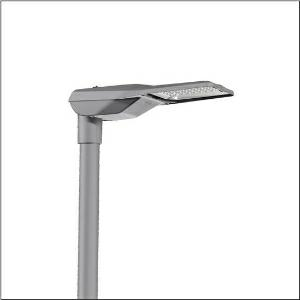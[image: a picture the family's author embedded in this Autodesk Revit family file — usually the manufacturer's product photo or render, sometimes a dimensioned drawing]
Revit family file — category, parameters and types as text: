
# Revit family: streetlight_sl_21_mini___pl52_5xe2h43s08hb_f567
name_source: partatom
category: Lighting Fixtures
units: mm (PartAtom-declared; Revit-internal decimal feet)

## family parameters
Cut with Voids When Loaded = No
Host = Face
Light Source = No
Part Type = Normal
Room Calculation Point = No
Round Connector Dimension = Use Diameter
Shared = No

## types (1)
- --- (1 x LED, 9260 lm, 66 W, 4000K)
    Apparent Load = 66 VA
    CIE Flux Codes = 27 59 98 100 100
    Color Rendering = 70
    Color Temperature = 4000K
    Default Elevation = 1800 mm
    Description = Streetlight SL 21 mini, mast luminaire, primary light control with lens, of PMMA, primary optical cover: cover, of toughened safety glass, transparent, light distribution: PL52, light emission: direct distribution, primary light characteristic: asymmetric, installation type: side-entry, post-top, LED, High Power LED, rated luminous flux: 9.260lm, luminous efficacy: 140lm/W, light colour: 740, colour temperature: 4000K, control gear: D4i, control: overheat protection, constant luminous flux control, time-dependent luminous flux control, flexible luminous flux parameterisation, pre-setting: logarithmic dimming characteristic, mains connection: 220..240V, AC, 50/60Hz, start of lifetime: 66W, end of service life: 69W, reduction: 30W, luminaire housing, of diecast aluminium, powder-coated, Siteco® metallic grey (DB 702S), corrosivity category C5 mid according to DIN EN ISO 12944, please order mast flange separately, inclination adjustable: 0°, 5°, 10°, 15°, sealing non-destructively replaceable, multi-level sealing system, length: 628mm, width: 235mm, height: 110mm, mast flange for spigot size: 42mm (side-entry): 5XC10008XM4, 60/48mm (side-entry/post-top): 5XC10108XM2, 76/60mm (side-entry/post-top): 5XC10108XM1, mounting height: 4..8m, Smart Interface above, protection rating (complete): IP66, insulation class (complete): insulation class II (safety insulation), certification: CE, ENEC, ENEC+, VDE, impact resistance: IK10, permissible operating ambient temperature for outdoor applications: -40..+50°C, standard-compliant lighting for roads and squares, packaging unit: 1 piece

Light Distribution: PL52
    Height = 110 mm
    Lamp = 1 x LED
    Lamp Light Flux = 9260 lm
    Lamp Power = 66 W
    Lamp count = 1
    Length = 625 mm
    Luminous efficacy = 140 lm/W
    Manufacturer = Siteco
    ModVariant = No
    Model = 5XE2H43S08HB
    Number of Poles = 1
    OnlyDefault = Yes
    Power Factor = 1
    Product Name = Streetlight SL 21 mini | PL52
    Product group = mast luminaire | pylon top
    ProductGroupID = 6100
    Protection Class = Protection class II
    Protection Degree = IP 66
    RLX_Detail_Level = 1
    RLX_Emergency_Light_Flux = 0 lm
    RLX_Emergency_Type = 0
    RLX_Emergency_Type_DB = No
    RlxData = <blob elided: 35705 chars, md5=6d88856d>
    Socket = socket
    Standby Power = 0 W
    System Light Flux = 9260 lm
    System Power = 66 W
    Type Comments = factory setting: luminous flux: 100 % | dim-lin: 254 | 670 mA
    Type Image = l_1003515.jpg
    URL = http://relux.com
    VarID = @adj_211395
    Voltage = 0 V
    Weight = 0.00 kg
    Width = 234 mm

## geometry (parser evidence)
native form markers: Blend x4, Sweep x9
no freeform markers — native parametric forms only
